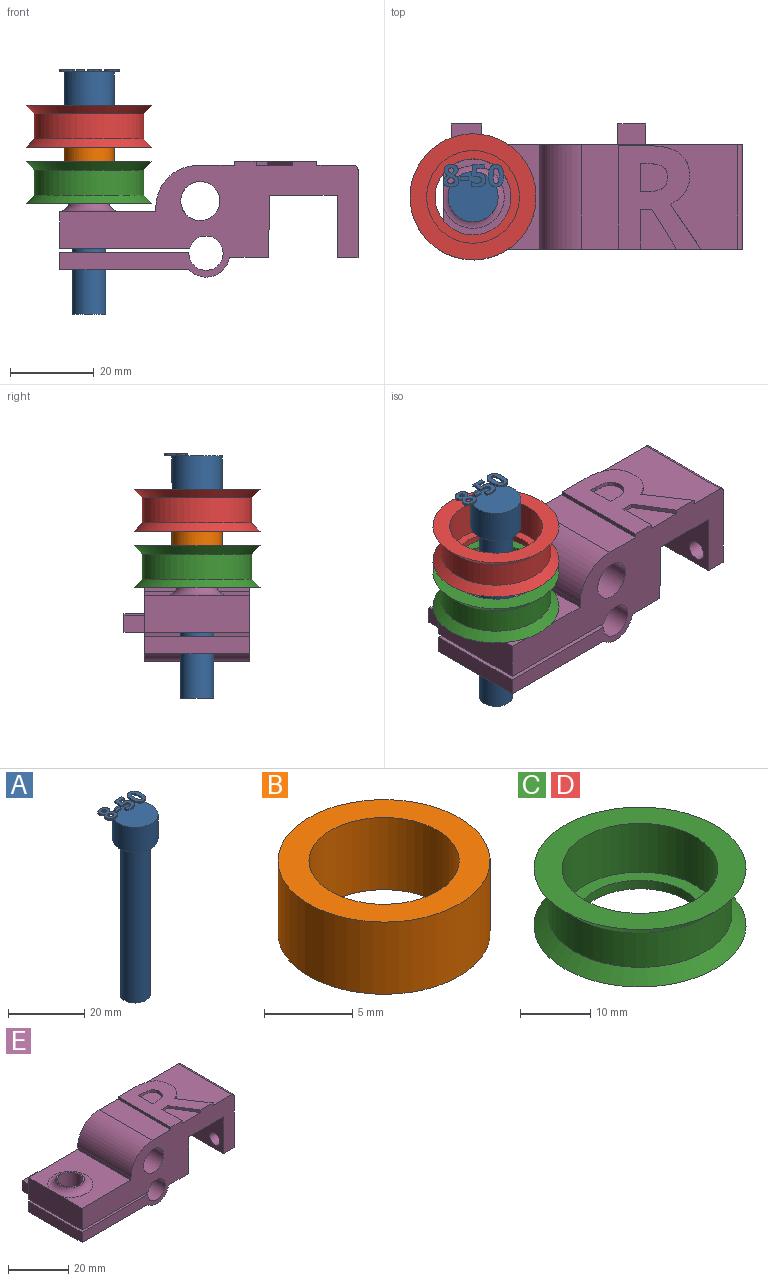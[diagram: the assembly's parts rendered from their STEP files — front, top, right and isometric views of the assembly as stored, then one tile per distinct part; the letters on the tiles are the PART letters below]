
ASSEMBLY  parts=5 mates=4
PART A: 86 faces, bbox 14.5x13.7x58.5 mm
  f0: plane 12x12mm, normal (0,0,1), area 99.4mm2, adj f5,f22,f23,f24,f25,f26,f40,f41
  f1: plane 1x0.26mm, normal (0,0,1), area 0.1mm2, adj f5,f46,f47,f48,f49
  f2: plane 0.85x0.68mm, normal (0,0,1), area 0.2mm2, adj f5,f29,f30,f31
  f3: cylinder r=4mm len=50mm, axis (0,0,-1), area 1256.6mm2, adj f4,f6
  f4: plane 8x8mm, normal (0,0,-1), area 50.3mm2, adj f3
  f5: cylinder r=6mm len=12mm, axis (0,0,-1), area 301.6mm2, adj f0,f1,f2,f6,f39,f45,f67,f85
  f6: plane 12x12mm, normal (0,0,-1), area 62.8mm2, adj f3,f5
  f7: extruded ~0.5x0.46mm, area 0.2mm2, adj f8,f37,f38,f39
  f8: extruded ~0.5x0.46mm, area 0.2mm2, adj f7,f9,f38,f39
  f9: extruded ~0.5x0.39mm, area 0.2mm2, adj f8,f10,f38,f39
  f10: extruded ~0.5x0.4mm, area 0.2mm2, adj f9,f11,f38,f39
  f11: extruded ~0.5x0.49mm, area 0.3mm2, adj f10,f12,f38,f39
  f12: extruded ~0.5x0.5mm, area 0.3mm2, adj f11,f13,f38,f39
  f13: extruded ~0.5x0.39mm, area 0.2mm2, adj f12,f37,f38,f39
  f14: extruded ~1.22x0.5mm, area 0.6mm2, adj f15,f35,f38,f39
  f15: extruded ~1.22x0.5mm, area 0.6mm2, adj f14,f16,f38,f39
  f16: extruded ~0.91x0.5mm, area 0.5mm2, adj f15,f17,f38,f39
  f17: extruded ~0.71x0.5mm, area 0.4mm2, adj f16,f18,f38,f39
  f18: extruded ~0.65x0.61mm, area 0.4mm2, adj f17,f19,f38,f39
  f19: extruded ~0.77x0.62mm, area 0.5mm2, adj f18,f20,f38,f39
  f20: extruded ~0.8x0.5mm, area 0.4mm2, adj f19,f21,f38,f39
  f21: extruded ~1.04x0.5mm, area 0.6mm2, adj f20,f22,f38,f39
  f22: extruded ~1.36x0.5mm, area 0.7mm2, adj f0,f21,f23,f38,f39
  f23: extruded ~1.33x0.5mm, area 0.7mm2, adj f0,f22,f24,f38
  f24: extruded ~1.04x0.51mm, area 0.6mm2, adj f0,f23,f25,f38
  f25: extruded ~0.75x0.5mm, area 0.4mm2, adj f0,f24,f26,f38
  f26: extruded ~0.85x0.66mm, area 0.5mm2, adj f0,f25,f27,f38,f39
  f27: extruded ~0.72x0.56mm, area 0.5mm2, adj f26,f28,f38,f39
  f28: extruded ~0.72x0.5mm, area 0.4mm2, adj f27,f35,f38,f39
  f29: extruded ~0.5x0.45mm, area 0.3mm2, adj f2,f30,f36,f38,f39
  f30: extruded ~0.5x0.47mm, area 0.3mm2, adj f2,f29,f31,f38
  f31: extruded ~0.62x0.5mm, area 0.3mm2, adj f2,f30,f32,f38,f39
  f32: extruded ~0.59x0.5mm, area 0.3mm2, adj f31,f33,f38,f39
  f33: extruded ~0.5x0.48mm, area 0.3mm2, adj f32,f34,f38,f39
  f34: extruded ~0.89x0.77mm, area 0.6mm2, adj f33,f36,f38,f39
  f35: extruded ~0.93x0.5mm, area 0.5mm2, adj f14,f28,f38,f39
  f36: extruded ~0.66x0.5mm, area 0.4mm2, adj f29,f34,f38,f39
  f37: extruded ~0.5x0.39mm, area 0.2mm2, adj f7,f13,f38,f39
  f38: plane 5.4x3.69mm, normal (0,0,1), area 12.7mm2, adj f7,f8,f9,f10,f11,f12,f13,f14
  f39: plane 5.4x3.53mm, normal (0,0,-1), area 10.2mm2, adj f5,f7,f8,f9,f10,f11,f12,f13
  f40: plane 0.9x0.5mm, normal (-1,0,0), area 0.4mm2, adj f0,f41,f43,f44
  f41: plane 1.93x0.5mm, normal (0,-1,0), area 1mm2, adj f0,f40,f42,f44
  f42: plane 0.9x0.5mm, normal (1,0,0), area 0.4mm2, adj f0,f41,f43,f44
  f43: plane 1.93x0.5mm, normal (0,1,0), area 1mm2, adj f0,f40,f42,f44
  f44: plane 1.93x0.9mm, normal (0,0,1), area 1.7mm2, adj f40,f41,f42,f43
  f45: plane 0.76x0.31mm, normal (0,0,-1), area 0mm2, adj f5,f46
  f46: extruded ~1.21x0.5mm, area 0.7mm2, adj f0,f1,f45,f47,f65,f66
  f47: extruded ~0.54x0.5mm, area 0.3mm2, adj f1,f46,f48,f66
  f48: plane 0.5x0.13mm, normal (-0.2,0.98,0), area 0.1mm2, adj f1,f47,f49,f66
  f49: plane 1.03x0.5mm, normal (1,-0.09,0), area 0.5mm2, adj f1,f48,f50,f66,f67
  f50: plane 1.88x0.5mm, normal (0,-1,0), area 0.9mm2, adj f49,f51,f66,f67
  f51: plane 0.94x0.5mm, normal (1,0,0), area 0.5mm2, adj f50,f52,f66,f67
  f52: plane 2.85x0.5mm, normal (0,1,0), area 1.4mm2, adj f51,f53,f66,f67
  f53: plane 2.68x0.5mm, normal (-1,0.07,0), area 1.3mm2, adj f0,f52,f54,f66,f67
  f54: plane 0.5x0.44mm, normal (-0.47,-0.88,0), area 0.3mm2, adj f0,f53,f55,f66
  f55: extruded ~0.5x0.37mm, area 0.2mm2, adj f0,f54,f56,f66
  f56: extruded ~0.5x0.42mm, area 0.2mm2, adj f0,f55,f57,f66
  f57: extruded ~1.05x0.8mm, area 0.8mm2, adj f0,f56,f58,f66
  f58: extruded ~1.02x0.83mm, area 0.8mm2, adj f0,f57,f59,f66
  f59: extruded ~0.72x0.5mm, area 0.4mm2, adj f0,f58,f60,f66
  f60: extruded ~0.66x0.5mm, area 0.4mm2, adj f0,f59,f61,f66
  f61: plane 0.96x0.5mm, normal (-1,0,0), area 0.5mm2, adj f0,f60,f62,f66
  f62: extruded ~1.42x0.5mm, area 0.7mm2, adj f0,f61,f63,f66
  f63: extruded ~1.55x0.5mm, area 0.8mm2, adj f0,f62,f64,f66
  f64: extruded ~1.36x0.54mm, area 0.8mm2, adj f0,f63,f65,f66
  f65: extruded ~1.17x0.5mm, area 0.6mm2, adj f0,f46,f64,f66
  f66: plane 5.33x3.51mm, normal (0,0,1), area 10.9mm2, adj f46,f47,f48,f49,f50,f51,f52,f53
  f67: plane 2.97x1.71mm, normal (0,0,-1), area 3.5mm2, adj f5,f49,f50,f51,f52,f53
  f68: extruded ~1.39x0.5mm, area 0.7mm2, adj f69,f83,f84,f85
  f69: extruded ~1.39x0.5mm, area 0.7mm2, adj f68,f70,f84,f85
  f70: extruded ~0.56x0.5mm, area 0.4mm2, adj f69,f71,f84,f85
  f71: extruded ~0.56x0.5mm, area 0.4mm2, adj f70,f72,f84,f85
  f72: extruded ~1.39x0.5mm, area 0.7mm2, adj f71,f73,f84,f85
  f73: extruded ~1.38x0.5mm, area 0.7mm2, adj f72,f74,f84,f85
  f74: extruded ~0.56x0.5mm, area 0.4mm2, adj f73,f83,f84,f85
  f75: extruded ~2.04x0.5mm, area 1.1mm2, adj f76,f82,f84,f85
  f76: extruded ~2.02x0.5mm, area 1.1mm2, adj f75,f77,f84,f85
  f77: extruded ~1.38x0.69mm, area 0.8mm2, adj f76,f78,f84,f85
  f78: extruded ~1.38x0.66mm, area 0.8mm2, adj f77,f79,f84,f85
  f79: extruded ~2.05x0.5mm, area 1.1mm2, adj f78,f80,f84,f85
  f80: extruded ~2.02x0.5mm, area 1mm2, adj f0,f79,f81,f84,f85
  f81: extruded ~1.37x0.68mm, area 0.8mm2, adj f0,f80,f82,f84
  f82: extruded ~1.39x0.66mm, area 0.8mm2, adj f0,f75,f81,f84,f85
  f83: extruded ~0.56x0.5mm, area 0.4mm2, adj f68,f74,f84,f85
  f84: plane 5.41x3.68mm, normal (0,0,1), area 12.1mm2, adj f68,f69,f70,f71,f72,f73,f74,f75
  f85: plane 5.41x3.68mm, normal (0,0,-1), area 10.3mm2, adj f5,f68,f69,f70,f71,f72,f73,f74
PART B: 4 faces, bbox 12x12x5 mm
  f0: cylinder r=4.25mm len=8.5mm, axis (0,0,-1), area 133.5mm2, adj f2,f3
  f1: cylinder r=6mm len=12mm, axis (0,0,-1), area 188.5mm2, adj f2,f3
  f2: plane 12x12mm, normal (0,0,1), area 56.4mm2, adj f0,f1
  f3: plane 12x12mm, normal (0,0,-1), area 56.4mm2, adj f0,f1
PART C: 8 faces, bbox 30.2x30.2x10 mm
  f0: plane 30.2x30.2mm, normal (0,0,1), area 329.2mm2, adj f1,f7
  f1: cylinder r=11.1mm len=22.2mm, axis (0,0,-1), area 592.8mm2, adj f0,f2
  f2: plane 22.2x22.2mm, normal (0,0,1), area 126.9mm2, adj f1,f3
  f3: cylinder r=9.1mm len=18.2mm, axis (0,0,-1), area 85.8mm2, adj f2,f4
  f4: plane 30.2x30.2mm, normal (0,0,-1), area 456.2mm2, adj f3,f5
  f5: cone r=13.1mm half-angle=45deg, axis (0,0,-1), area 250.6mm2, adj f4,f6
  f6: cylinder r=13.1mm len=26.2mm, axis (0,0,-1), area 493.9mm2, adj f5,f7
  f7: cone r=15.1mm half-angle=45deg, axis (0,0,1), area 250.6mm2, adj f0,f6
PART D: same geometry as C
PART E: 56 faces, bbox 74.9x30x27.7 mm
  f0: plane 37.42x25mm, normal (0,0,1), area 542.1mm2, adj f14,f15,f25,f27,f40,f41,f42,f43
  f1: plane 9.51x8.71mm, normal (0,0,1), area 54.7mm2, adj f14,f37,f38,f39
  f2: plane 25x4.12mm, normal (-1,0,0), area 103mm2, adj f5,f14,f15,f19
  f3: cylinder r=4.17mm len=8.35mm, axis (0,0,1), area 108.1mm2, adj f5,f19
  f4: plane 25x9.34mm, normal (0,0,-1), area 233.4mm2, adj f13,f14,f15,f17
  f5: plane 30.88x25mm, normal (0,0,-1), area 717.2mm2, adj f2,f3,f14,f15,f17
  f6: plane 25x8.82mm, normal (-1,0,0), area 219.6mm2, adj f7,f14,f15,f20,f24
  f7: plane 25x23mm, normal (0,0,1), area 400mm2, adj f6,f8,f14,f15,f24
  f8: plane 25x1.1mm, normal (-1,0,0), area 27.5mm2, adj f7,f14,f15,f25
  f9: plane 25x21.09mm, normal (1,0,0), area 493.5mm2, adj f10,f14,f15,f22,f23,f27
  f10: plane 25x5mm, normal (0,0,-1), area 125mm2, adj f9,f11,f14,f15
  f11: plane 25x15mm, normal (-1,0,0), area 341.3mm2, adj f10,f12,f14,f15,f22,f23
  f12: plane 25x16.2mm, normal (0,0,-1), area 405mm2, adj f11,f13,f14,f15
  f13: plane 25x14.91mm, normal (1,0,-0.01), area 372.8mm2, adj f4,f12,f14,f15
  f14: plane 71.42x27.75mm, normal (0,-1,0), area 1040.4mm2, adj f0,f1,f2,f4,f5,f6,f7,f8
  f15: plane 71.42x26.75mm, normal (0,1,0), area 969.3mm2, adj f0,f2,f4,f5,f6,f7,f8,f9
  f16: cylinder r=4.17mm len=10.78mm, axis (0,0,1), area 282.8mm2, adj f20,f21
  f17: cylinder r=5.75mm len=25mm, axis (0,-1,0), area 315.9mm2, adj f4,f5,f14,f15
  f18: cylinder r=4.1mm len=25mm, axis (0,-1,0), area 618.7mm2, adj f14,f15,f19,f20
  f19: plane 30.91x25mm, normal (0,0,1), area 718.1mm2, adj f2,f3,f14,f15,f18
  f20: plane 31.07x30mm, normal (0,0,-1), area 758.4mm2, adj f6,f14,f15,f16,f18,f29,f30,f31
  f21: plane 9.35x9.35mm, normal (0,0,1), area 13.9mm2, adj f16,f24
  f22: cylinder r=2.43mm len=5mm, axis (1,0,0), area 76.2mm2, adj f9,f11
  f23: cylinder r=2.2mm len=5mm, axis (1,0,0), area 69.1mm2, adj f9,f11
  f24: torus R=7.5mm, axis (0,0,-1), area 134.6mm2, adj f6,f7,f21
  f25: cylinder r=10mm len=25mm, axis (0,-1,0), area 392.7mm2, adj f0,f8,f14,f15
  f26: cylinder r=4.68mm len=25mm, axis (0,-1,0), area 735.2mm2, adj f14,f15
  f27: cylinder r=1mm len=25mm, axis (0,-1,0), area 39.3mm2, adj f0,f9,f14,f15
  f28: plane 7.3x5mm, normal (0,0,1), area 36.5mm2, adj f15,f29,f30,f31
  f29: plane 5x4.12mm, normal (-1,0,0), area 20.6mm2, adj f15,f20,f28,f31
  f30: plane 5x4.12mm, normal (1,0,0), area 20.6mm2, adj f15,f20,f28,f31
  f31: plane 7.3x4.12mm, normal (0,1,0), area 30.1mm2, adj f20,f28,f29,f30
  f32: plane 6.63x5mm, normal (0,0,1), area 33.2mm2, adj f15,f33,f35,f36
  f33: plane 5x4.5mm, normal (-1,0,0), area 22.5mm2, adj f15,f32,f34,f36
  f34: plane 6.63x5mm, normal (0,0,-1), area 33.2mm2, adj f15,f33,f35,f36
  f35: plane 5x4.5mm, normal (1,0,0), area 22.5mm2, adj f15,f32,f34,f36
  f36: plane 6.63x4.5mm, normal (0,1,0), area 29.9mm2, adj f32,f33,f34,f35
  f37: plane 9.51x1mm, normal (1,0,0), area 9.5mm2, adj f1,f14,f38,f54
  f38: plane 2.79x1mm, normal (0,-1,0), area 2.8mm2, adj f1,f37,f39,f54
  f39: plane 9.51x5.92mm, normal (-0.85,-0.53,0), area 11.2mm2, adj f1,f14,f38,f54
  f40: extruded ~10.8x7.29mm, area 13mm2, adj f0,f14,f41,f54
  f41: extruded ~3.41x2.67mm, area 4.4mm2, adj f0,f40,f42,f54
  f42: extruded ~3.89x1.2mm, area 4.1mm2, adj f0,f41,f43,f54
  f43: extruded ~5.59x2.42mm, area 6.3mm2, adj f0,f42,f44,f54
  f44: extruded ~7.48x1.84mm, area 7.8mm2, adj f0,f43,f45,f54
  f45: plane 7.22x1mm, normal (0,1,0), area 7.2mm2, adj f0,f44,f46,f54
  f46: plane 24.79x1mm, normal (-1,0,0), area 24.8mm2, adj f0,f14,f45,f54
  f47: plane 1.69x1mm, normal (0,1,0), area 1.7mm2, adj f48,f53,f54,f55
  f48: plane 6.7x1mm, normal (1,0,0), area 6.7mm2, adj f47,f49,f54,f55
  f49: plane 1.6x1mm, normal (0,-1,0), area 1.6mm2, adj f48,f50,f54,f55
  f50: extruded ~3.75x1mm, area 3.9mm2, adj f49,f51,f54,f55
  f51: extruded ~2.51x1.21mm, area 2.9mm2, adj f50,f52,f54,f55
  f52: extruded ~2.61x1.19mm, area 3mm2, adj f51,f53,f54,f55
  f53: extruded ~3.68x1mm, area 3.8mm2, adj f47,f52,f54,f55
  f54: plane 24.79x19.8mm, normal (0,0,1), area 300mm2, adj f14,f37,f38,f39,f40,f41,f42,f43
  f55: plane 6.7x6.56mm, normal (0,0,1), area 38.8mm2, adj f47,f48,f49,f50,f51,f52,f53
PLACE A t=(-103.78,-12.5,-13.6)mm
PLACE B rot(axis=(1,0,0),180deg) t=(-103.78,-12.5,26.4)mm
PLACE C t=(-103.78,-12.5,18.1)mm
PLACE D t=(-103.78,-12.5,31.6)mm
PLACE E at identity
MATE fastened A.f3 <-> D.f1  axis (0,0,-1) through (-103.78,-12.5,36.4)mm
MATE fastened B.f0 <-> C.f1  axis (0,0,1) through (-103.78,-12.5,21.4)mm
MATE fastened C.f1 <-> E.f3  axis (0,0,-1) through (-103.78,-12.5,12.9)mm
MATE fastened D.f1 <-> B.f0  axis (0,0,-1) through (-103.78,-12.5,26.4)mm
